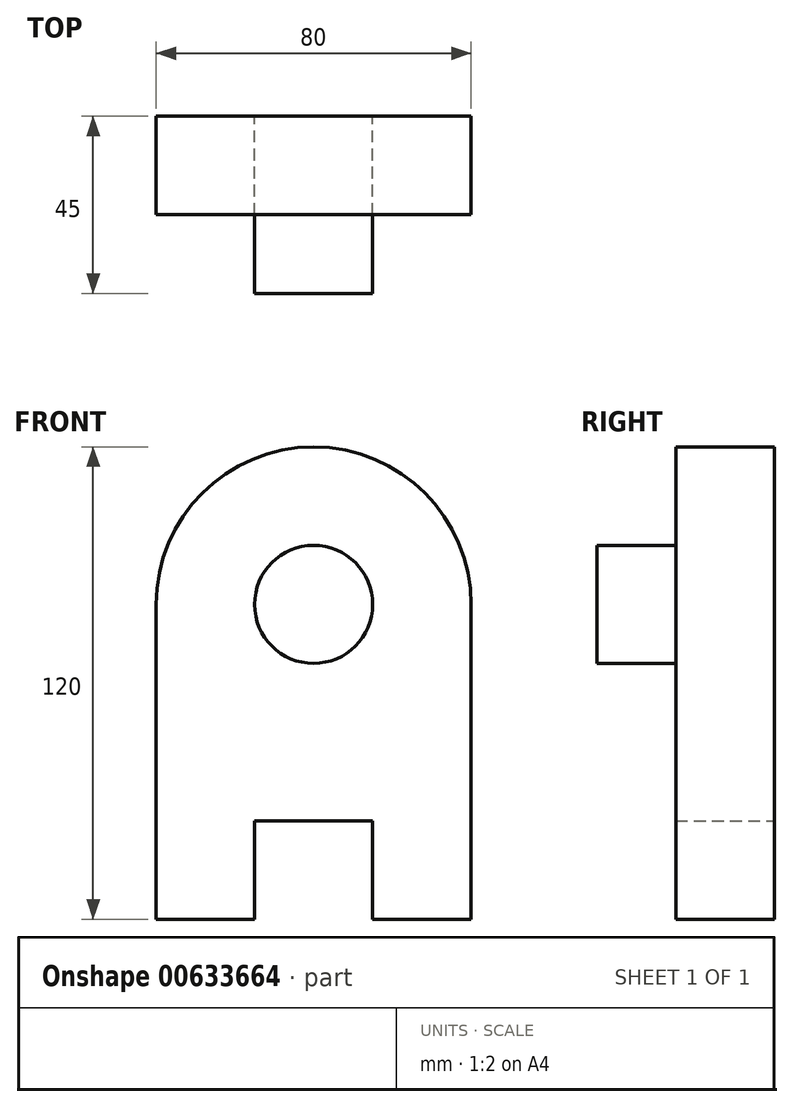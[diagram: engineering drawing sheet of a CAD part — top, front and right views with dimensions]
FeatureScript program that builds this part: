
annotation { "Feature Type Name" : "Feature", "Feature Type Description" : "" }
export const myFeature = defineFeature(function(context is Context, id is Id, definition is map)
    precondition{}
    {
        {
            var Q0;
            Q0=qCreatedBy(makeId("Front.planeOp"),FACE);
            var sketch = newSketch(context, id + "F0", { "sketchPlane" : qUnion([Q0])});
            skLineSegment(sketch, "E0.top", {"start": v(40, -40) * mm, "end": v(15, -40) * mm});
            skLineSegment(sketch, "E0.left", {"start": v(40, 40) * mm, "end": v(40, -40) * mm});
            skLineSegment(sketch, "E0.right", {"start": v(-40, 40) * mm, "end": v(-40, -40) * mm});
            skPoint(sketch, "E0.middle", {"position": v(0, 0) * mm});
            skArc(sketch, "E1", {"start": v(40, 40) * mm, "mid": v(0, 80) * mm, "end": v(-40, 40) * mm});
            skLineSegment(sketch, "E2.bottom", {"start": v(15, -15) * mm, "end": v(-15, -15) * mm});
            skLineSegment(sketch, "E2.left", {"start": v(15, -15) * mm, "end": v(15, -40) * mm});
            skLineSegment(sketch, "E2.right", {"start": v(-15, -15) * mm, "end": v(-15, -40) * mm});
            skPoint(sketch, "E2.middle", {"position": v(0, -40) * mm});
            skPoint(sketch, "E2.top.start.orphan", {"position": v(15, -65) * mm});
            skPoint(sketch, "E3.orphan", {"position": v(-15, -65) * mm});
            skLineSegment(sketch, "E4.trimOffspring", {"start": v(-15, -40) * mm, "end": v(-40, -40) * mm});
            skSolve(sketch);
        }
        {
            var Q0;
            Q0=makeQuery(id+"F0.imprint","IMPRINT",FACE,{"disambiguationData":[TD([[makeQuery(id+"F0.imprint","IMPRINT",EDGE,{"derivedFrom":sQuery(id+"F0.wireOp",EDGE,"E0.top")}),-1.0]])]});
            extrude(context, id + "F1", {"entities" : qUnion([Q0]), "depth" : 25 * mm, "offsetDistance" : 25 * mm});
        }
        {
            var Q0;
            Q0=makeQuery(id+"F1.opExtrude","CAP_FACE",FACE,{"disambiguationData":[OSD([sQuery(id+"F0.wireOp",EDGE,"E0.top"),sQuery(id+"F0.wireOp",EDGE,"E0.left"),sQuery(id+"F0.wireOp",EDGE,"E0.right"),sQuery(id+"F0.wireOp",EDGE,"E1"),sQuery(id+"F0.wireOp",EDGE,"E2.bottom"),sQuery(id+"F0.wireOp",EDGE,"E2.left"),sQuery(id+"F0.wireOp",EDGE,"E2.right"),sQuery(id+"F0.wireOp",EDGE,"E4.trimOffspring")])],"isStart":false});
            var sketch = newSketch(context, id + "F2", { "sketchPlane" : qUnion([Q0])});
            skCircle(sketch, "E5", {"center": v(0, 40) * mm, "radius": 15 * mm});
            skSolve(sketch);
        }
        {
            var Q0;
            Q0=makeQuery(id+"F2.imprint","IMPRINT",FACE,{"disambiguationData":[TD([[makeQuery(id+"F2.imprint","IMPRINT",EDGE,{"derivedFrom":sQuery(id+"F2.wireOp",EDGE,"E5")}),1.0]])]});
            extrude(context, id + "F3", {"entities" : qUnion([Q0]), "operationType" : NewBodyOperationType.ADD, "depth" : 20 * mm, "offsetDistance" : 25 * mm});
        }
    });
